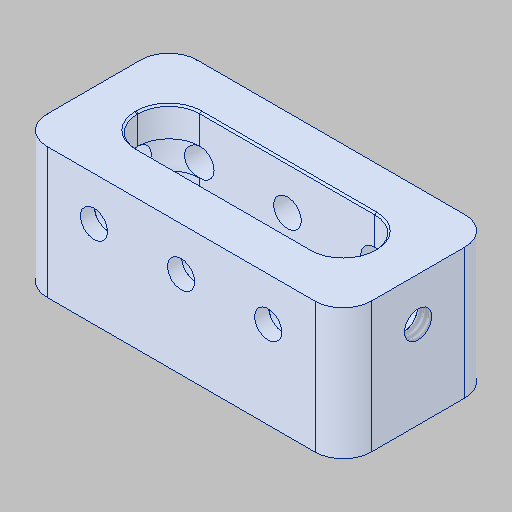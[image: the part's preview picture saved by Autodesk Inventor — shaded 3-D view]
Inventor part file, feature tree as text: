
AUTODESK INVENTOR PART (.ipt)
format: ipt  version: 2023.4 (Build 274418000, 418)  size: 355,840 bytes
history: native  units: in
note: dims shown in document units (in); Inventor stores cm internally (conversion verified against a paired STEP export)
features: sketch x4, hole x3, projected_geometry x2, extrude x1, chamfer x1
ambient origin geometry x8: Origin, YZ Plane, XZ Plane, XY Plane, X Axis, Y Axis, Z Axis, Center Point
bodies: Solid1 (feature_tree)
feature tree (11):
  extrude  "Extrusion1"  Depth=1.0in TaperAngle=0.0deg
  hole  "Hole1"  [1 undecoded]
  hole  "Hole2"  [1 undecoded]
  hole  "Hole3"  [1 undecoded]
  sketch  "Sketch1"  dims[d0=0.0625in d1=1.0in d2=0.0in]
  projected_geometry  "Projected Loop1"
  sketch  "Sketch2"  dims[d3=0.156in d4=0.38in d5=0.385in d6=0.25in d7=0.563in d8=1.0in d9=0.8108in]
  projected_geometry  "Projected Loop2"
  sketch  "Sketch3"  dims[d10=0.196in d11=0.5in d12=0.375in d13=0.25in d14=0.5635in d15=1.0in d16=0.8108in]
  sketch  "Sketch4"  dims[d17=0.156in d18=0.38in d19=0.385in d20=0.25in d21=0.563in d22=1.0in d23=0.8108in]
  chamfer  "Chamfer2"  [1 undecoded]
note: 4 required parameter values undecoded (feature->parameter linkage not recoverable at this tier; creation-order binding heuristic only, values carry confidence <= 0.55)
